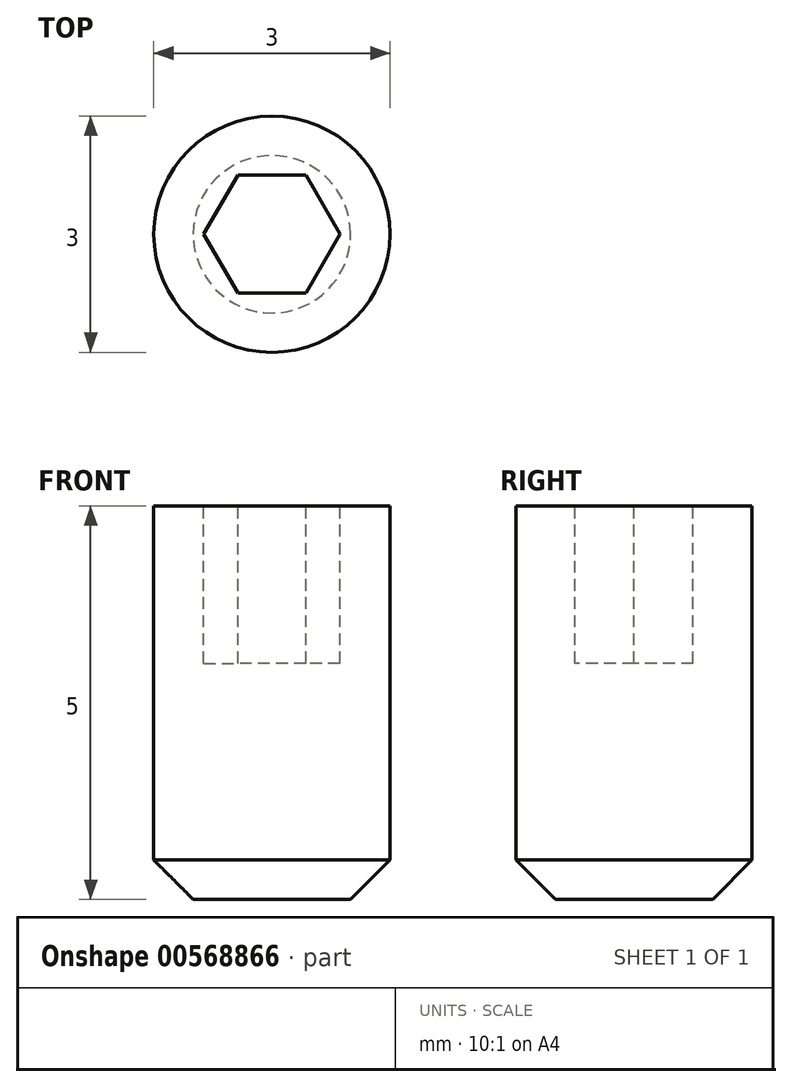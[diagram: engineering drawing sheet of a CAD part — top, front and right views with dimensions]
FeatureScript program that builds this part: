
annotation { "Feature Type Name" : "Feature", "Feature Type Description" : "" }
export const myFeature = defineFeature(function(context is Context, id is Id, definition is map)
    precondition{}
    {
        {
            var Q0;
            Q0=qCreatedBy(makeId("Front.planeOp"),FACE);
            var sketch = newSketch(context, id + "F0", { "sketchPlane" : qUnion([Q0])});
            skLineSegment(sketch, "E0", {"start": v(0, 8.76) * mm, "end": v(0, -7.02) * mm, "construction": true});
            skLineSegment(sketch, "E1", {"start": v(-1.5, 0) * mm, "end": v(-1.5, 5) * mm});
            skLineSegment(sketch, "E2", {"start": v(-1.5, 5) * mm, "end": v(0, 5) * mm});
            skLineSegment(sketch, "E3", {"start": v(-1.5, 0) * mm, "end": v(0, 0) * mm});
            skLineSegment(sketch, "E4", {"start": v(0, 0) * mm, "end": v(0, 5) * mm});
            skSolve(sketch);
        }
        {
            var Q0;
            Q0 = qSketchRegion(id + "F0", true);
            var Q1;
            Q1=sQuery(id+"F0.wireOp",EDGE,"E0");
            revolve(context, id + "F1", {"entities" : qUnion([Q0]), "axis" : qUnion([Q1]), "revolveType" : RevolveType.FULL});
        }
        {
            var Q0;
            Q0=makeQuery(id+"F1.opRevolve","SWEPT_EDGE",EDGE,{"disambiguationData":[OSD([sQuery(id+"F0.wireOp",EDGE,"E1"),sQuery(id+"F0.wireOp",EDGE,"E3")])]});
            chamfer(context, id + "F2", {"entities" : qUnion([Q0]), "width" : 0.5 * mm, "tangentPropagation" : true});
        }
        {
            var Q0;
            Q0=makeQuery(id+"F1.opRevolve","SWEPT_FACE",FACE,{"disambiguationData":[OSD([sQuery(id+"F0.wireOp",EDGE,"E2")])]});
            var sketch = newSketch(context, id + "F3", { "sketchPlane" : qUnion([Q0])});
            skCircle(sketch, "E5.0", {"center": v(0, 0) * mm, "radius": 1.5 * mm, "construction": true});
            skCircle(sketch, "E6.cCircle", {"center": v(0, 0) * mm, "radius": 0.75 * mm, "construction": true});
            skLineSegment(sketch, "E6.0", {"start": v(0.43, -0.75) * mm, "end": v(-0.43, -0.75) * mm});
            skLineSegment(sketch, "E6.1", {"start": v(-0.43, -0.75) * mm, "end": v(-0.87, 0) * mm});
            skLineSegment(sketch, "E6.2", {"start": v(-0.87, 0) * mm, "end": v(-0.43, 0.75) * mm});
            skLineSegment(sketch, "E6.3", {"start": v(-0.43, 0.75) * mm, "end": v(0.43, 0.75) * mm});
            skLineSegment(sketch, "E6.4", {"start": v(0.43, 0.75) * mm, "end": v(0.87, 0) * mm});
            skLineSegment(sketch, "E6.5", {"start": v(0.87, 0) * mm, "end": v(0.43, -0.75) * mm});
            skPoint(sketch, "E6.0.midPoint", {"position": v(0, -0.75) * mm});
            skSolve(sketch);
        }
        {
            var Q0;
            Q0=makeQuery(id+"F3.imprint","IMPRINT",FACE,{"disambiguationData":[TD([[makeQuery(id+"F3.imprint","IMPRINT",EDGE,{"derivedFrom":sQuery(id+"F3.wireOp",EDGE,"E6.0")}),-1.0]])]});
            extrude(context, id + "F4", {"entities" : qUnion([Q0]), "operationType" : NewBodyOperationType.REMOVE, "oppositeDirection" : true, "depth" : 2 * mm, "offsetDistance" : 25 * mm});
        }
    });
